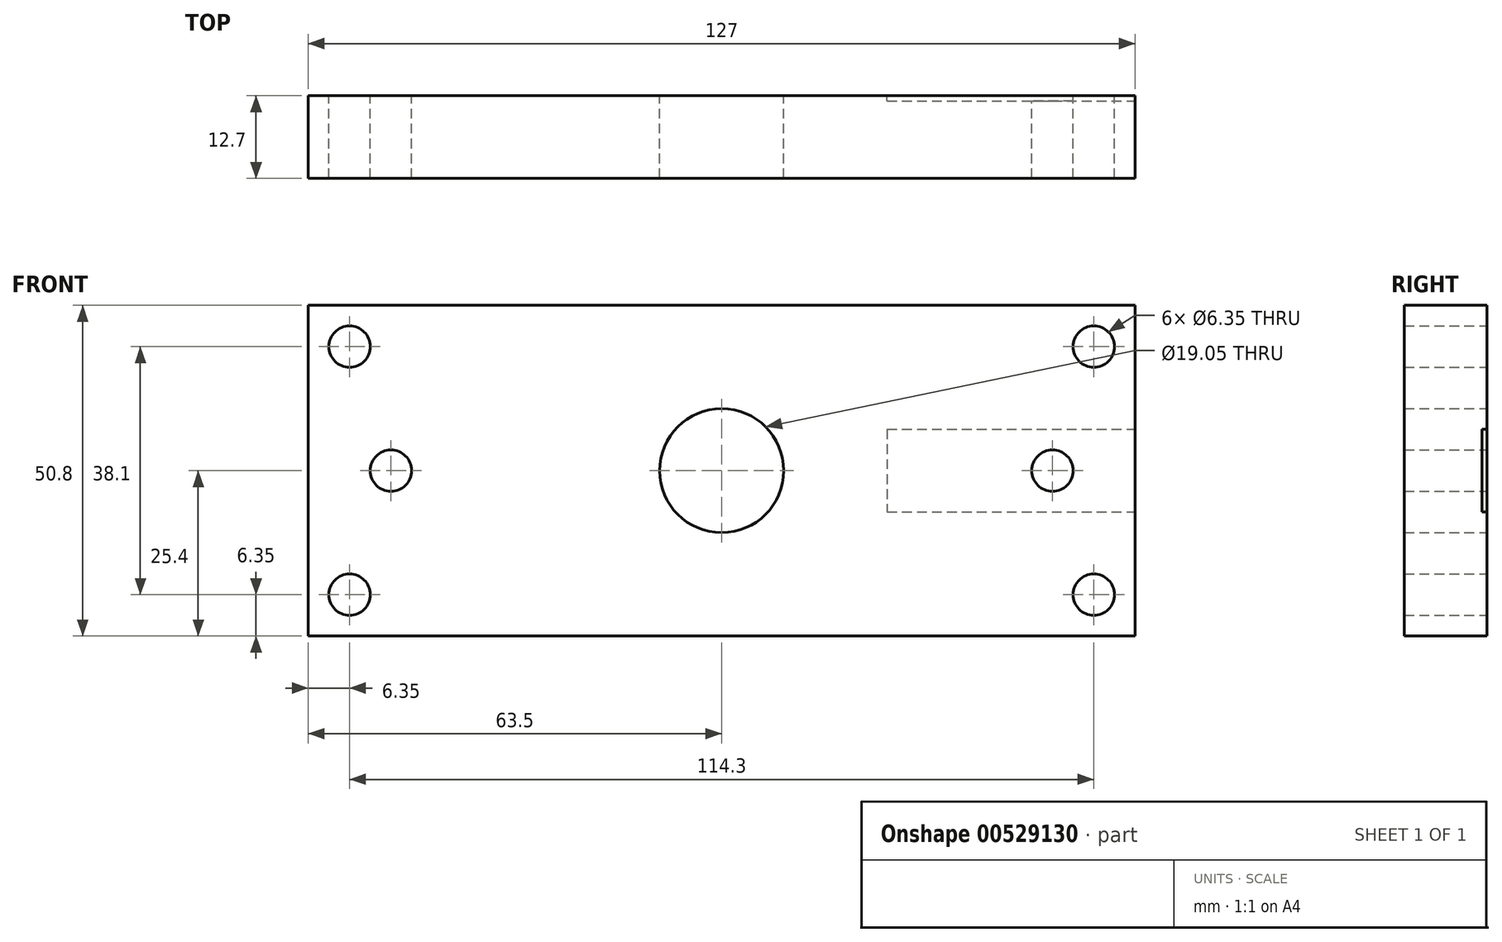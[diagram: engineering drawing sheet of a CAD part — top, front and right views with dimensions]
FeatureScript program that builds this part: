
annotation { "Feature Type Name" : "Feature", "Feature Type Description" : "" }
export const myFeature = defineFeature(function(context is Context, id is Id, definition is map)
    precondition{}
    {
        {
            var Q0;
            Q0=qCreatedBy(makeId("Front.planeOp"),FACE);
            var sketch = newSketch(context, id + "F0", { "sketchPlane" : qUnion([Q0])});
            skLineSegment(sketch, "E0.bottom", {"start": v(-63.5, 25.4) * mm, "end": v(63.5, 25.4) * mm});
            skLineSegment(sketch, "E0.top", {"start": v(-63.5, -25.4) * mm, "end": v(63.5, -25.4) * mm});
            skLineSegment(sketch, "E0.left", {"start": v(-63.5, 25.4) * mm, "end": v(-63.5, -25.4) * mm});
            skLineSegment(sketch, "E0.right", {"start": v(63.5, 25.4) * mm, "end": v(63.5, -25.4) * mm});
            skPoint(sketch, "E0.middle", {"position": v(0, 0) * mm});
            skCircle(sketch, "E1", {"center": v(0, 0) * mm, "radius": 9.53 * mm});
            skLineSegment(sketch, "E2", {"start": v(0, 9.53) * mm, "end": v(0, -9.53) * mm, "construction": true});
            skLineSegment(sketch, "E3", {"start": v(7.1, 6.35) * mm, "end": v(63.5, 6.35) * mm, "construction": true});
            skLineSegment(sketch, "E4", {"start": v(7.1, -6.35) * mm, "end": v(63.5, -6.35) * mm, "construction": true});
            skLineSegment(sketch, "E5", {"start": v(7.1, 6.35) * mm, "end": v(63.5, 6.35) * mm});
            skLineSegment(sketch, "E6", {"start": v(7.1, -6.35) * mm, "end": v(63.5, -6.35) * mm});
            skLineSegment(sketch, "E7", {"start": v(0, -25.4) * mm, "end": v(0, 25.4) * mm, "construction": true});
            skLineSegment(sketch, "E8", {"start": v(-57.15, 25.4) * mm, "end": v(-57.15, -25.4) * mm, "construction": true});
            skLineSegment(sketch, "E9", {"start": v(-63.5, -19.05) * mm, "end": v(63.5, -19.05) * mm, "construction": true});
            skLineSegment(sketch, "E10.MirrorCS", {"start": v(-57.15, -25.4) * mm, "end": v(-57.15, 25.4) * mm, "construction": true});
            skLineSegment(sketch, "E11.MirrorCS", {"start": v(-63.5, 19.05) * mm, "end": v(63.5, 19.05) * mm, "construction": true});
            skCircle(sketch, "E12", {"center": v(-57.15, 19.05) * mm, "radius": 3.18 * mm});
            skCircle(sketch, "E13", {"center": v(57.15, 19.05) * mm, "radius": 3.18 * mm});
            skCircle(sketch, "E14.MirrorC", {"center": v(-57.15, -19.05) * mm, "radius": 3.18 * mm});
            skCircle(sketch, "E15.MirrorC", {"center": v(57.15, -19.05) * mm, "radius": 3.18 * mm});
            skPoint(sketch, "E16.startSnap0", {"position": v(0, 19.05) * mm});
            skCircle(sketch, "E17", {"center": v(50.8, 0) * mm, "radius": 3.18 * mm});
            skCircle(sketch, "E18.MirrorC", {"center": v(-50.8, 0) * mm, "radius": 3.18 * mm});
            skLineSegment(sketch, "E19", {"start": v(25.4, 6.35) * mm, "end": v(25.4, -6.35) * mm, "construction": true});
            skLineSegment(sketch, "E20", {"start": v(25.4, 6.35) * mm, "end": v(25.4, -6.35) * mm});
            skLineSegment(sketch, "E21", {"start": v(9.52, 0) * mm, "end": v(63.5, 0) * mm, "construction": true});
            skSolve(sketch);
        }
        {
            var Q0;
            Q0 = qSketchRegion(id + "F0", true);
            var Q1;
            {var subQ5=sQuery(id+"F0.wireOp",EDGE,"E20");Q1=makeQuery(id+"F0.imprint","IMPRINT",FACE,{"disambiguationData":[TD([[makeQuery(id+"F0.imprint","IMPRINT",EDGE,{"derivedFrom":subQ5}),-1.0]])]});}
            extrude(context, id + "F1", {"entities" : qUnion([Q0, Q1]), "depth" : 12.7 * mm, "offsetDistance" : 25.4 * mm});
        }
        {
            var Q0;
            Q0=makeQuery(id+"F0.imprint","IMPRINT",FACE,{"disambiguationData":[TD([[makeQuery(id+"F0.imprint","IMPRINT",EDGE,{"derivedFrom":sQuery(id+"F0.wireOp",EDGE,"E17")}),-1.0]])]});
            extrude(context, id + "F2", {"entities" : qUnion([Q0]), "operationType" : NewBodyOperationType.REMOVE, "depth" : 0.81 * mm, "offsetDistance" : 25.4 * mm});
        }
    });
